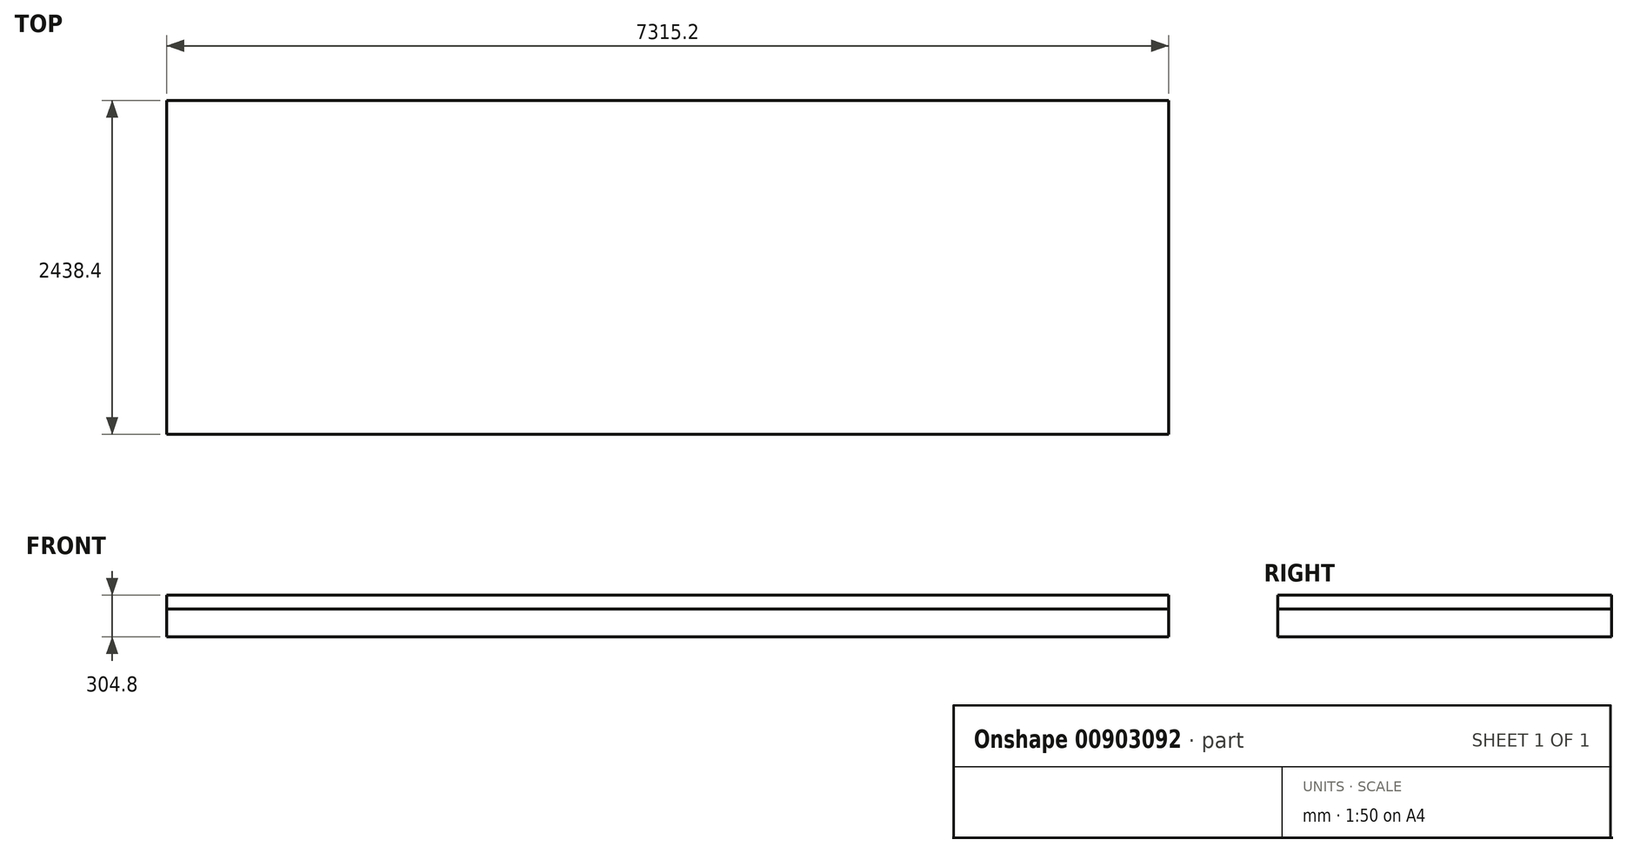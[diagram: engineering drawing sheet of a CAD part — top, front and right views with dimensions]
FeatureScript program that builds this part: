
annotation { "Feature Type Name" : "Feature", "Feature Type Description" : "" }
export const myFeature = defineFeature(function(context is Context, id is Id, definition is map)
    precondition{}
    {
        {
            var Q0;
            Q0=qCreatedBy(makeId("Top.planeOp"),FACE);
            var sketch = newSketch(context, id + "F0", { "sketchPlane" : qUnion([Q0])});
            skLineSegment(sketch, "E0.bottom", {"start": v(-2859.93, 1215.41) * mm, "end": v(4455.27, 1215.41) * mm});
            skLineSegment(sketch, "E0.top", {"start": v(-2859.93, -1222.99) * mm, "end": v(4455.27, -1222.99) * mm});
            skLineSegment(sketch, "E0.left", {"start": v(-2859.93, 1215.41) * mm, "end": v(-2859.93, -1222.99) * mm});
            skLineSegment(sketch, "E0.right", {"start": v(4455.27, 1215.41) * mm, "end": v(4455.27, -1222.99) * mm});
            skSolve(sketch);
        }
        {
            var Q0;
            Q0=makeQuery(id+"F0.imprint","IMPRINT",FACE,{"disambiguationData":[TD([[makeQuery(id+"F0.imprint","IMPRINT",EDGE,{"derivedFrom":sQuery(id+"F0.wireOp",EDGE,"E0.bottom")}),-1.0]])]});
            extrude(context, id + "F1", {"entities" : qUnion([Q0]), "oppositeDirection" : true, "depth" : 203.2 * mm, "offsetDistance" : 25.4 * mm});
        }
        {
            var Q0;
            Q0=makeQuery(id+"F1.opExtrude","CAP_FACE",FACE,{"disambiguationData":[OSD([sQuery(id+"F0.wireOp",EDGE,"E0.bottom"),sQuery(id+"F0.wireOp",EDGE,"E0.top"),sQuery(id+"F0.wireOp",EDGE,"E0.left"),sQuery(id+"F0.wireOp",EDGE,"E0.right")])],"isStart":true});
            extrude(context, id + "F2", {"entities" : qUnion([Q0]), "depth" : 101.6 * mm, "offsetDistance" : 25.4 * mm});
        }
    });
